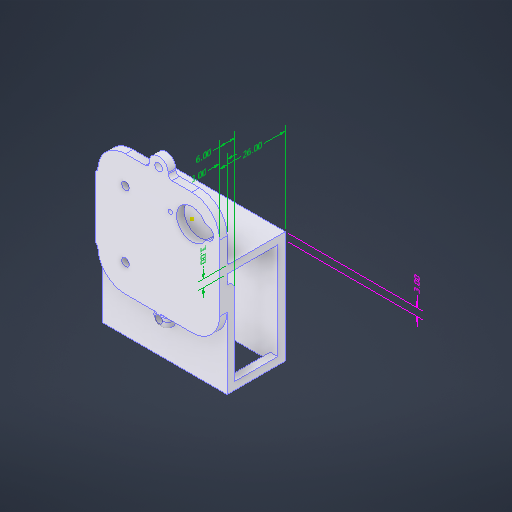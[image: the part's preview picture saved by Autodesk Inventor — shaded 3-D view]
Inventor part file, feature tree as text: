
AUTODESK INVENTOR PART (.ipt)
format: ipt  version: 2025.3 (Build 293356000, 356)  size: 430,080 bytes
history: native  units: in
note: dims shown in document units (in); Inventor stores cm internally (conversion verified against a paired STEP export)
features: extrude x13, sketch x11, other x7, fillet x5, direct_edit x3, move_body x3
ambient origin geometry x8: Origin, YZ Plane, XZ Plane, XY Plane, X Axis, Y Axis, Z Axis, Center Point
bodies: Solid1 (feature_tree)
feature tree (42):
  other  "Annotations"
  extrude  "Extrusion1"  Depth=0.0591in
  fillet  "Fillet1"  Radius=0.0591in
  fillet  "Fillet2"  Radius=0.9055in
  extrude  "Extrusion2"  Depth=1.0236in TaperAngle=0.0deg
  extrude  "Extrusion3"  Depth=0.0315in
  extrude  "Extrusion4"  Depth=1.0236in
  fillet  "Fillet3"  Radius=1.0236in
  extrude  "Extrusion5"  Depth=0.1181in
  direct_edit  "Direct Edit1"
  extrude  "Extrusion6"  Depth=0.2378in
  extrude  "Extrusion7"  TaperAngle=0.0deg  [1 undecoded]
  direct_edit  "Direct Edit2"
  direct_edit  "Direct Edit3"
  sketch  "Sketch10"  dims[d25=0.0in d26=0.0in d27=0.6413in d28=0.1181in]
  extrude  "Extrusion8"  Depth=0.3937in TaperAngle=0.0deg
  extrude  "Extrusion9"  TaperAngle=0.0deg  [1 undecoded]
  extrude  "Extrusion10"  Depth=0.1181in
  extrude  "Extrusion11"  TaperAngle=45.0deg  [1 undecoded]
  fillet  "Fillet4"  Radius=0.1181in
  extrude  "Extrusion12"  Depth=0.1181in
  fillet  "Fillet5"  [1 undecoded]
  extrude  "Extrusion13"  Depth=0.7874in TaperAngle=0.0deg
  sketch  "Sketch1"  dims[d0=0.1181in d1=0.2953in d2=0.1181in d3=0.0in d4=0.0591in d5=0.0591in d11=0.9055in d12=0.0in]
  sketch  "Sketch2"  dims[d13=1.0236in d14=0.0in d17=1.0236in d18=0.0in]
  sketch  "Sketch3"  dims[d19=0.0315in d20=0.0669in]
  sketch  "Sketch7"  dims[d21=0.515in d22=1.172in d23=1.0236in d24=0.0in]
  sketch  "Sketch11"  dims[d29=0.4134in d30=0.2378in]
  sketch  "Sketch12"  dims[d31=0.3762in d32=0.0in d33=0.0in]
  sketch  "Sketch13"  dims[d34=0.1793in d35=0.3937in d36=0.0in]
  sketch  "Sketch14"  dims[d40=0.0in d41=0.0in d42=0.0394in d43=0.0in d44=0.0in d45=-0.0394in]
  sketch  "Sketch15"  dims[d50=0.1181in d51=0.0in d58=0.1181in]
  sketch  "Sketch16"  dims[d64=0.7874in d65=0.0in d66=45.0deg d67=0.1181in d68=0.1181in d69=135.0deg d70=0.7874in d71=0.0in d72=0.8504in d73=0.1181in d74=0.2362in d75=0.7874in d76=0.0in d77=0.1181in d78=0.1181in d79=0.7874in d80=0.0in d81=0.1181in d84=0.1181in d85=1.5079in d86=0.0in d47=0.2862in d48=0.2809in d49=0.1181in d52=0.1865in d53=0.1902in d54=0.1181in d55=0.3167in d56=0.077in d57=0.1181in d59=0.0617in d60=0.0767in d61=0.2362in d62=0.158in d63=1.0236in d82=0.2288in d83=0.9685in d87=0.0197in d88=0.0344in]
  move_body  "Move1"
  move_body  "Move2"
  move_body  "Move3"
  other  "Linear Dimension 1"
  other  "Linear Dimension 2"
  other  "Linear Dimension 3"
  other  "Linear Dimension 4"
  other  "Linear Dimension 5"
  other  "Linear Dimension 6"
note: 4 required parameter values undecoded (feature->parameter linkage not recoverable at this tier; creation-order binding heuristic only, values carry confidence <= 0.55)
